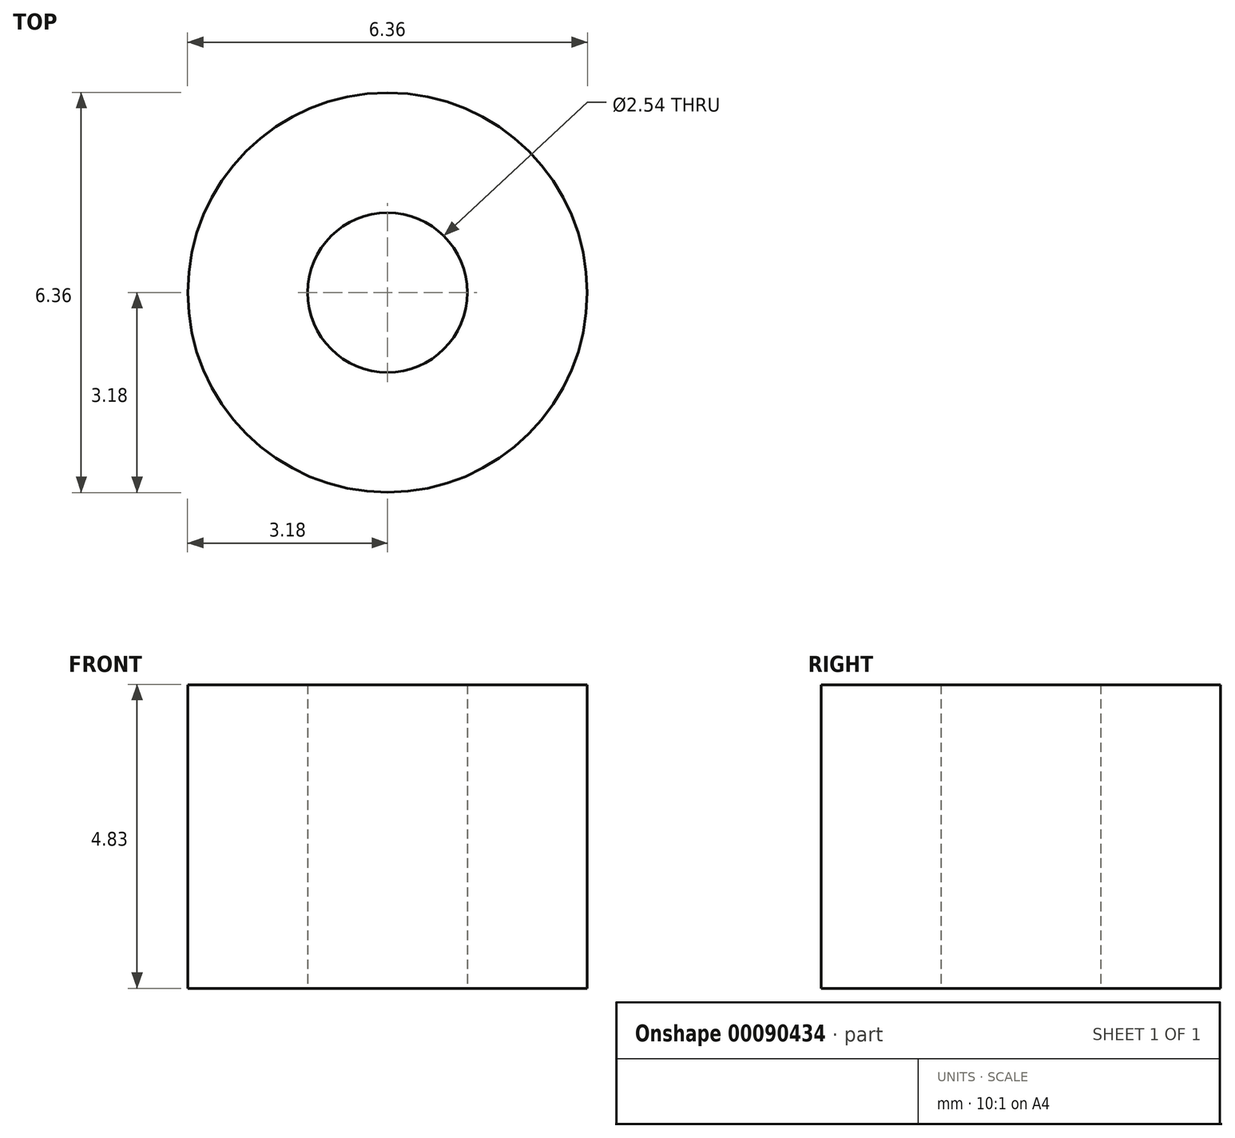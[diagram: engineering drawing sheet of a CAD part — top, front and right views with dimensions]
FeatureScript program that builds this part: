
annotation { "Feature Type Name" : "Feature", "Feature Type Description" : "" }
export const myFeature = defineFeature(function(context is Context, id is Id, definition is map)
    precondition{}
    {
        {
            var Q0;
            Q0=qCreatedBy(makeId("Top.planeOp"),FACE);
            var sketch = newSketch(context, id + "F0", { "sketchPlane" : qUnion([Q0])});
            skCircle(sketch, "E0", {"center": v(0, 0) * mm, "radius": 3.18 * mm});
            skCircle(sketch, "E1", {"center": v(0, 0) * mm, "radius": 1.27 * mm});
            skSolve(sketch);
        }
        {
            var Q0;
            Q0=makeQuery(id+"F0.imprint","IMPRINT",FACE,{"disambiguationData":[TD([[makeQuery(id+"F0.imprint","IMPRINT",EDGE,{"derivedFrom":sQuery(id+"F0.wireOp",EDGE,"E0")}),1.0]])]});
            extrude(context, id + "F1", {"entities" : qUnion([Q0]), "depth" : 4.83 * mm});
        }
    });
